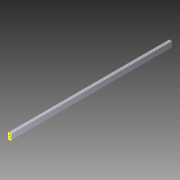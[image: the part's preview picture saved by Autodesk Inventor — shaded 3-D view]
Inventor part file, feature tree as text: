
AUTODESK INVENTOR PART (.ipt)
format: ipt  version: 2014 SP1 (Build 180222100, 222)  size: 784,896 bytes
history: native  units: in
note: dims shown in document units (in); Inventor stores cm internally (conversion verified against a paired STEP export)
features: other x2, sketch x1, imported_body x1
ambient origin geometry x8: Origin, YZ Plane, XZ Plane, XY Plane, X Axis, Y Axis, Z Axis, Center Point
bodies: Body1 (feature_tree)
feature tree (4):
  other  "Cut-Extrude2"
  other  "217-3453-STEP1"
  sketch  "Sketch1"
  imported_body  "Base1"
